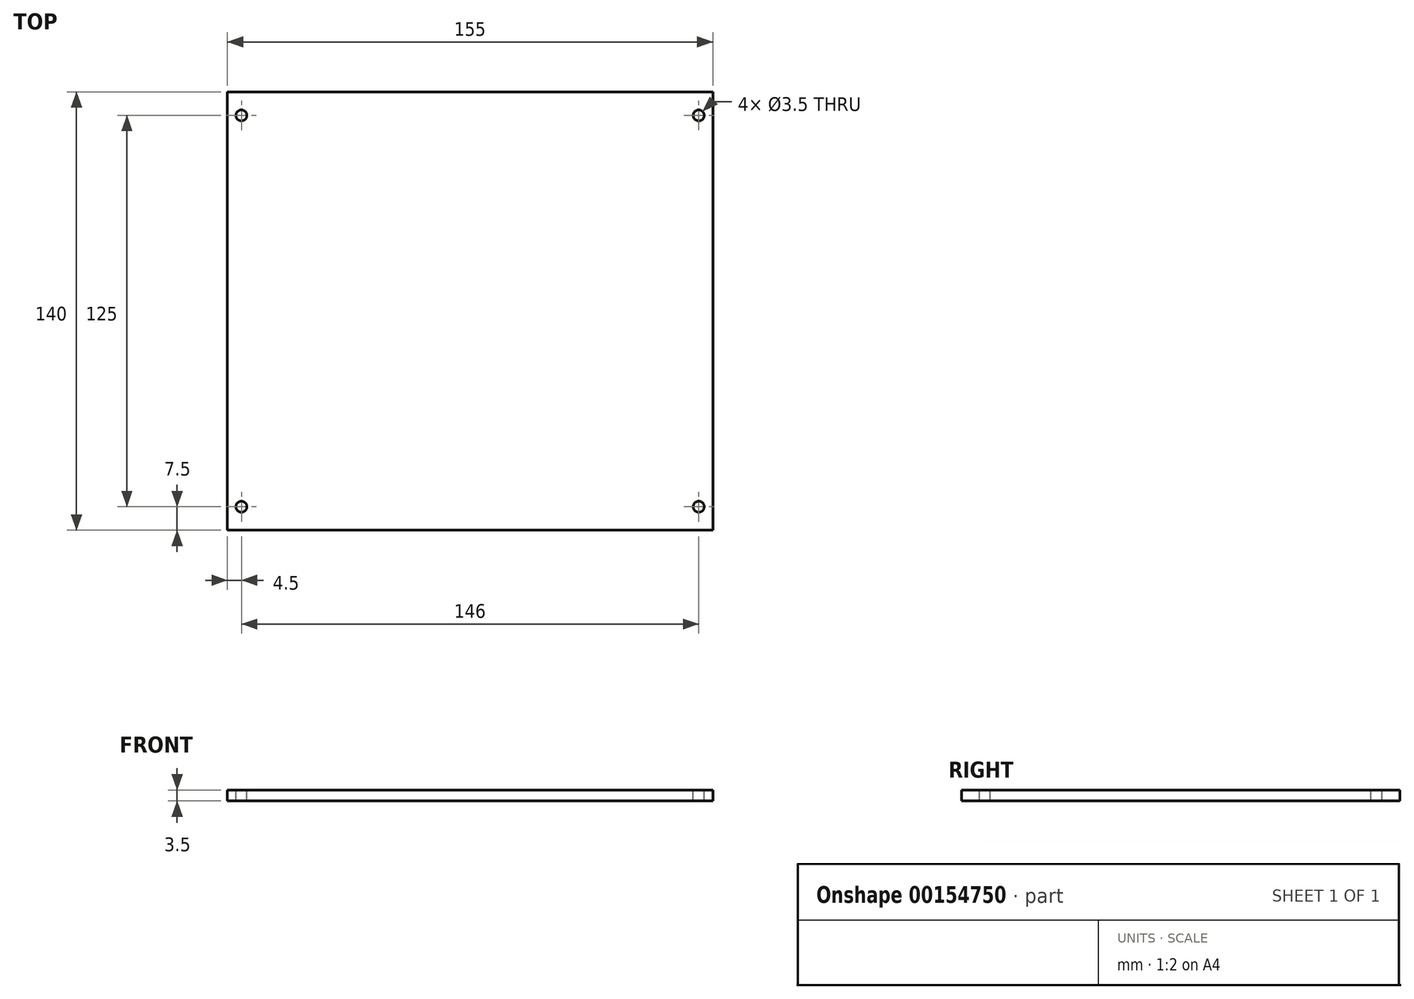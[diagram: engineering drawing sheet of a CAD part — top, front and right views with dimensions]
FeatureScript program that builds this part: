
annotation { "Feature Type Name" : "Feature", "Feature Type Description" : "" }
export const myFeature = defineFeature(function(context is Context, id is Id, definition is map)
    precondition{}
    {
        {
            var Q0;
            Q0=qCreatedBy(makeId("Top.planeOp"),FACE);
            var sketch = newSketch(context, id + "F0", { "sketchPlane" : qUnion([Q0])});
            skLineSegment(sketch, "E0.bottom", {"start": v(77.5, -70) * mm, "end": v(-77.5, -70) * mm});
            skLineSegment(sketch, "E0.top", {"start": v(77.5, 70) * mm, "end": v(-77.5, 70) * mm});
            skLineSegment(sketch, "E0.left", {"start": v(77.5, -70) * mm, "end": v(77.5, 70) * mm});
            skLineSegment(sketch, "E0.right", {"start": v(-77.5, -70) * mm, "end": v(-77.5, 70) * mm});
            skPoint(sketch, "E0.middle", {"position": v(0, 0) * mm});
            skSolve(sketch);
        }
        {
            var Q0;
            Q0 = qSketchRegion(id + "F0", true);
            extrude(context, id + "F1", {"entities" : qUnion([Q0]), "depth" : 3.5 * mm});
        }
        {
            var Q0;
            Q0=makeQuery(id+"F1.opExtrude","CAP_FACE",FACE,{"disambiguationData":[OSD([sQuery(id+"F0.wireOp",EDGE,"E0.bottom"),sQuery(id+"F0.wireOp",EDGE,"E0.top"),sQuery(id+"F0.wireOp",EDGE,"E0.left"),sQuery(id+"F0.wireOp",EDGE,"E0.right")])],"isStart":false});
            var sketch = newSketch(context, id + "F2", { "sketchPlane" : qUnion([Q0])});
            skCircle(sketch, "E1", {"center": v(-73, 62.5) * mm, "radius": 1.75 * mm});
            skCircle(sketch, "E2", {"center": v(73, 62.5) * mm, "radius": 1.75 * mm});
            skLineSegment(sketch, "E3", {"start": v(0, 0) * mm, "end": v(-44.5, 0) * mm});
            skCircle(sketch, "E4.MirrorC", {"center": v(-73, -62.5) * mm, "radius": 1.75 * mm});
            skCircle(sketch, "E5.MirrorC", {"center": v(73, -62.5) * mm, "radius": 1.75 * mm});
            skSolve(sketch);
        }
        {
            var Q0;
            Q0 = qSketchRegion(id + "F2", true);
            extrude(context, id + "F3", {"entities" : qUnion([Q0]), "operationType" : NewBodyOperationType.REMOVE, "endBound" : BoundingType.THROUGH_ALL, "oppositeDirection" : true, "depth" : 25 * mm});
        }
    });
